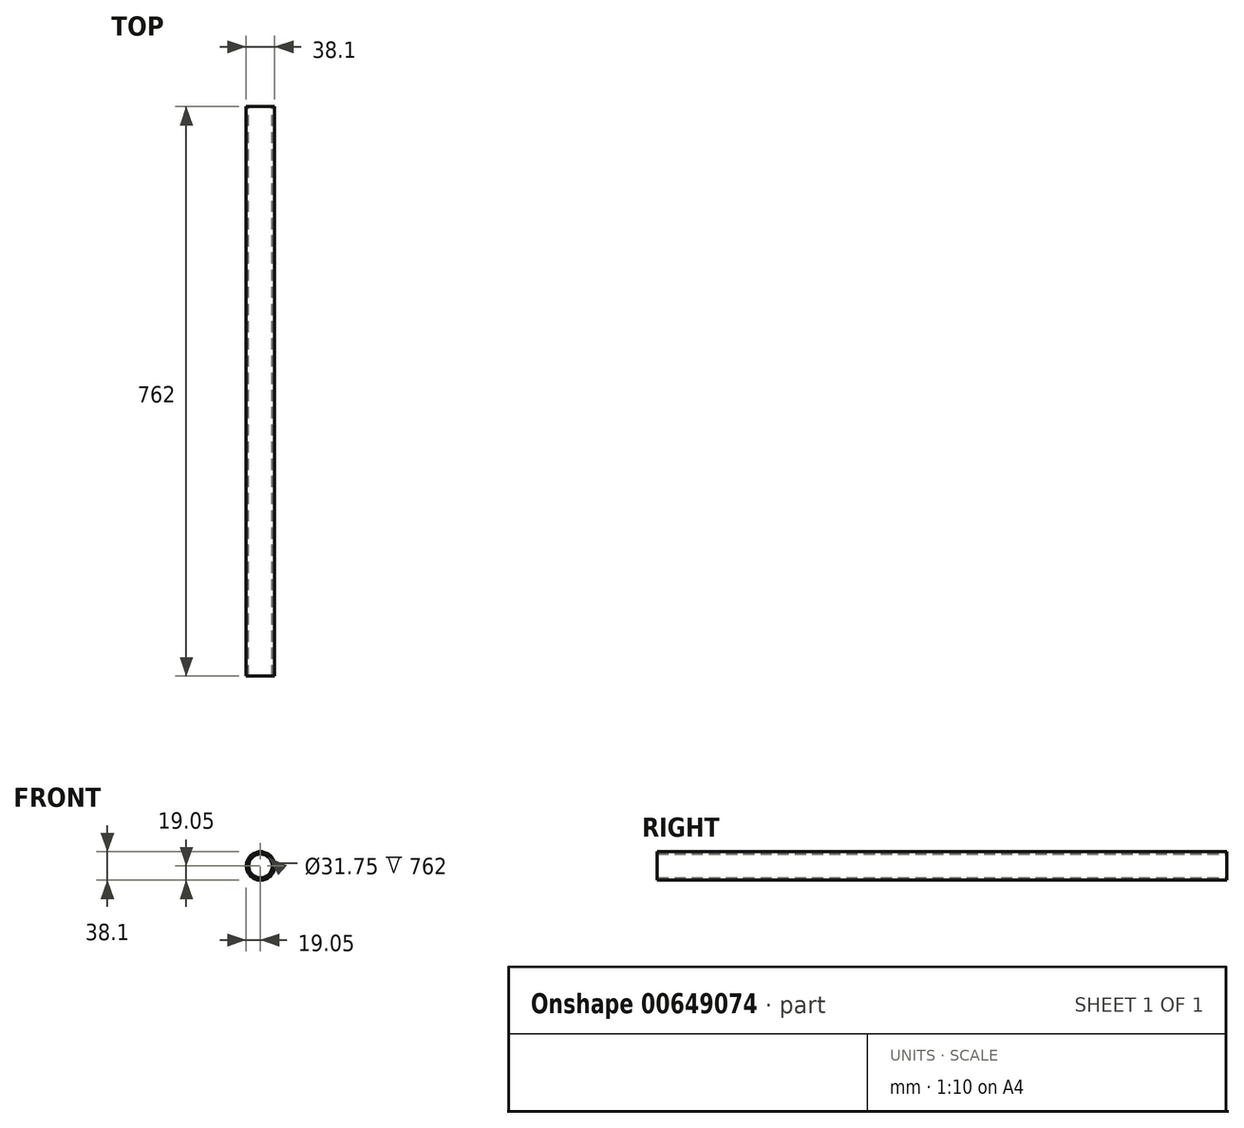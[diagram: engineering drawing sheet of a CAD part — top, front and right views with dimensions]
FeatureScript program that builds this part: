
annotation { "Feature Type Name" : "Feature", "Feature Type Description" : "" }
export const myFeature = defineFeature(function(context is Context, id is Id, definition is map)
    precondition{}
    {
        {
            var Q0;
            Q0=qCreatedBy(makeId("Front.planeOp"),FACE);
            var sketch = newSketch(context, id + "F0", { "sketchPlane" : qUnion([Q0])});
            skCircle(sketch, "E0", {"center": v(0, 0) * mm, "radius": 19.05 * mm});
            skCircle(sketch, "E1", {"center": v(0, 0) * mm, "radius": 15.88 * mm});
            skSolve(sketch);
        }
        {
            var Q0;
            Q0 = qSketchRegion(id + "F0", true);
            extrude(context, id + "F1", {"entities" : qUnion([Q0]), "depth" : 762 * mm, "offsetDistance" : 25.4 * mm});
        }
    });
